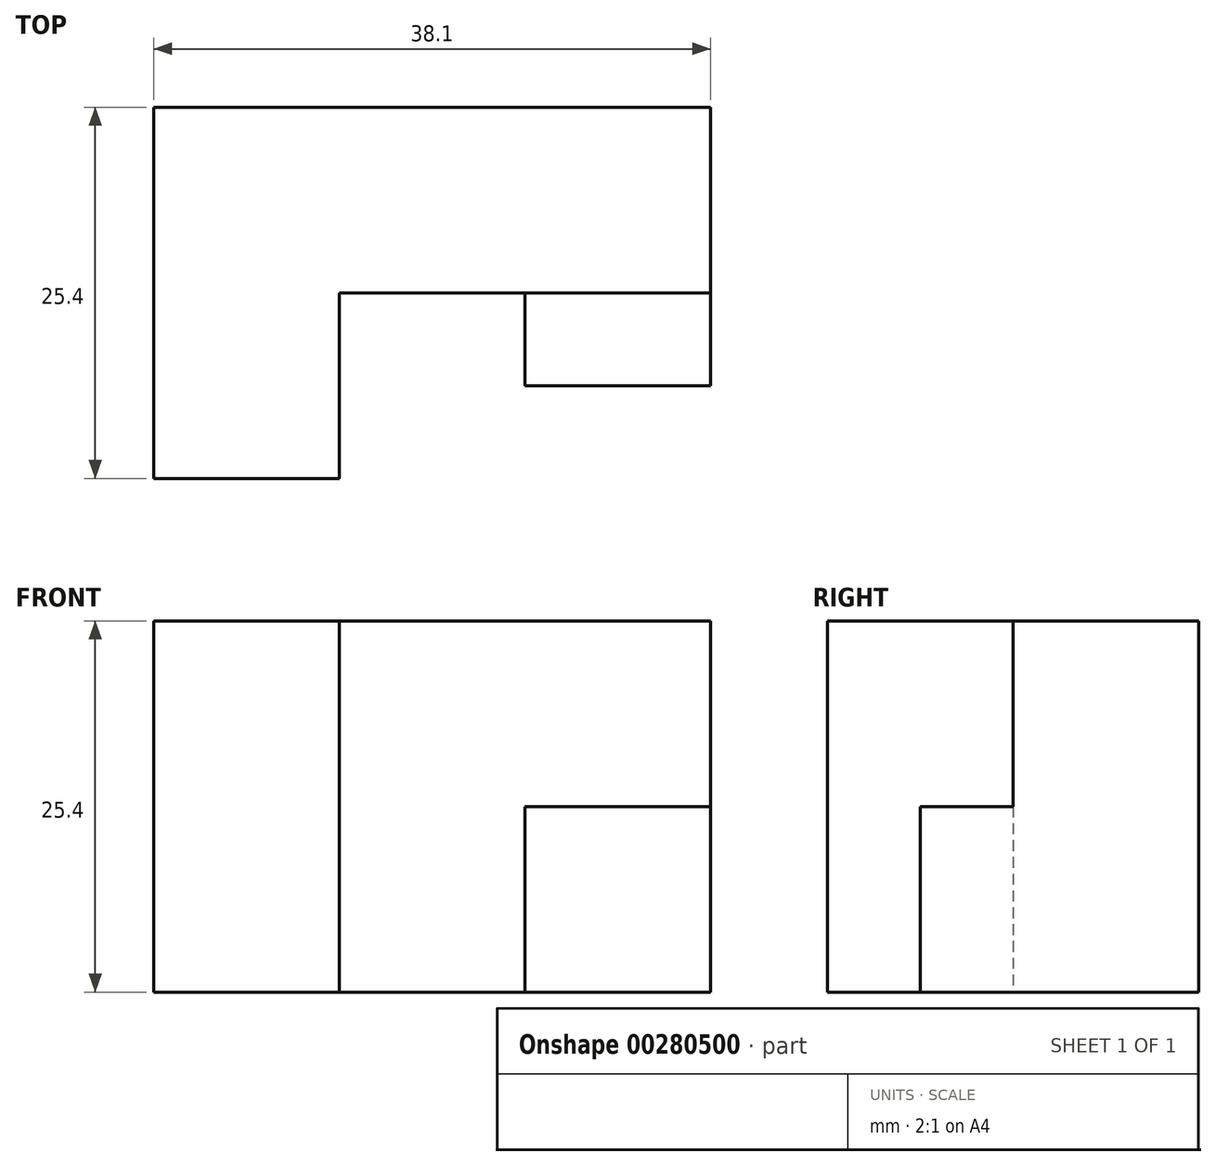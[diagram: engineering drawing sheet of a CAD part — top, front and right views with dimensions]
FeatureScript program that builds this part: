
annotation { "Feature Type Name" : "Feature", "Feature Type Description" : "" }
export const myFeature = defineFeature(function(context is Context, id is Id, definition is map)
    precondition{}
    {
        {
            var Q0;
            Q0=qCreatedBy(makeId("Front.planeOp"),FACE);
            var sketch = newSketch(context, id + "F0", { "sketchPlane" : qUnion([Q0])});
            skLineSegment(sketch, "E0", {"start": v(-19.05, 0) * mm, "end": v(19.05, 0) * mm});
            skLineSegment(sketch, "E1", {"start": v(-19.05, 0) * mm, "end": v(-19.05, 25.4) * mm});
            skLineSegment(sketch, "E2", {"start": v(-19.05, 25.4) * mm, "end": v(-6.35, 25.4) * mm});
            skLineSegment(sketch, "E3", {"start": v(-6.35, 25.4) * mm, "end": v(-6.35, 0) * mm});
            skLineSegment(sketch, "E4", {"start": v(-6.35, 25.4) * mm, "end": v(19.05, 25.4) * mm});
            skLineSegment(sketch, "E5", {"start": v(19.05, 25.4) * mm, "end": v(19.05, 12.7) * mm});
            skLineSegment(sketch, "E6", {"start": v(19.05, 12.7) * mm, "end": v(6.35, 12.7) * mm});
            skLineSegment(sketch, "E7", {"start": v(6.35, 12.7) * mm, "end": v(6.35, 0) * mm});
            skLineSegment(sketch, "E8", {"start": v(19.05, 12.7) * mm, "end": v(19.05, 0) * mm});
            skSolve(sketch);
        }
        {
            var Q0;
            {var subQ0=sQuery(id+"F0.wireOp",EDGE,"E1");Q0=makeQuery(id+"F0.imprint","IMPRINT",FACE,{"disambiguationData":[TD([[makeQuery(id+"F0.imprint","IMPRINT",EDGE,{"derivedFrom":subQ0}),-1.0]])]});}
            var Q1;
            {var subQ0=sQuery(id+"F0.wireOp",EDGE,"E3");Q1=makeQuery(id+"F0.imprint","IMPRINT",FACE,{"disambiguationData":[TD([[makeQuery(id+"F0.imprint","IMPRINT",EDGE,{"derivedFrom":subQ0}),1.0]])]});}
            var Q2;
            Q2=makeQuery(id+"F0.imprint","IMPRINT",FACE,{"disambiguationData":[TD([[makeQuery(id+"F0.imprint","IMPRINT",EDGE,{"derivedFrom":sQuery(id+"F0.wireOp",EDGE,"E6")}),1.0]])]});
            extrude(context, id + "F1", {"entities" : qUnion([Q0, Q1, Q2]), "oppositeDirection" : true, "depth" : 12.7 * mm});
        }
        {
            var Q0;
            {var subQ0=sQuery(id+"F0.wireOp",EDGE,"E1");Q0=makeQuery(id+"F0.imprint","IMPRINT",FACE,{"disambiguationData":[TD([[makeQuery(id+"F0.imprint","IMPRINT",EDGE,{"derivedFrom":subQ0}),-1.0]])]});}
            extrude(context, id + "F2", {"entities" : qUnion([Q0]), "operationType" : NewBodyOperationType.ADD, "depth" : 12.7 * mm});
        }
        {
            var Q0;
            Q0=makeQuery(id+"F0.imprint","IMPRINT",FACE,{"disambiguationData":[TD([[makeQuery(id+"F0.imprint","IMPRINT",EDGE,{"derivedFrom":sQuery(id+"F0.wireOp",EDGE,"E6")}),1.0]])]});
            extrude(context, id + "F3", {"entities" : qUnion([Q0]), "operationType" : NewBodyOperationType.ADD, "depth" : 6.35 * mm});
        }
    });
